# Revit family: Eurolan_Шкафы Rackcnet S3000
name_source: partatom
category: Электрооборудование
units: mm (PartAtom-declared; Revit-internal decimal feet)

## family parameters
Всегда вертикально = Да
На основе рабочей плоскости = Нет
Общий = Нет
При загрузке вырезать с полостями = Нет
Размер круглого соединителя = Использовать диаметр
Тип детали = Другая панель
Точка расчета площади = Нет

## types (64) — shared parameters
ADSK_Единица измерения = шт.
ADSK_Завод-изготовитель = Eurolan
ADSK_Количество фаз = 1
ADSK_Марка = S3000
ADSK_Материал = Металл RAL 9005
ADSK_Наименование краткое = 19'' шкаф Racknet S3000
ADSK_Напряжение = 230 В
Смещение от пола = 51 мм

## per-type parameters (varying)
| type | 33U | 42U | 47U | ADSK_Код изделия | ADSK_Масса | ADSK_Наименование | ADSK_Размер_Высота | ADSK_Размер_Глубина | ADSK_Размер_Ширина | Глубина зоны обслуживания_Сзади | Глубина зоны обслуживания_Спереди | выбор_задняя дверь | выбор_передняя дверь | число_передняя дверь |
| 22U__600 × 600_60F-22-66-30BL_19'' шкаф Racknet S3000 22U 600 × 600, передняя дверь металлическая одностворчатая, задняя дверь металлическая одностворчатая, черный | Нет | Нет | Нет | 60F-42-8A-30BL | 145 | 19'' шкаф Racknet S3000 42U 800 × 1000, передняя дверь металлическая одностворчатая, задняя дверь металлическая двустворчатая, черный | 1145 мм | 649 мм | 593 мм | 296.5 мм | 593 мм | in_Дверь_металлическая_одностворчатая | in_Дверь_металлическая_двустворчатая | 1 |
| 22U__600 × 600_60F-22-66-31BL_19'' шкаф Racknet S3000 22U 600 × 600, передняя дверь стеклянная одностворчатая, задняя дверь металлическая одностворчатая, черный | Нет | Нет | Нет | 60F-22-66-31BL | 64 | 19'' шкаф Racknet S3000 22U 600 × 600, передняя дверь стеклянная одностворчатая, задняя дверь металлическая одностворчатая, черный | 1145 мм | 649 мм | 593 мм | 296.5 мм | 593 мм | in_Дверь_металлическая_одностворчатая | in_Дверь_стеклянная_одностворчатая | 1 |
| 22U__600 × 600_60F-22-66-34BL_19'' шкаф Racknet S3000 22U 600 × 600, передняя дверь перфорированная одностворчатая, задняя дверь перфорированная одностворчатая, черный | Нет | Нет | Нет | 60F-22-66-34BL | 64 | 19'' шкаф Racknet S3000 22U 600 × 600, передняя дверь перфорированная одностворчатая, задняя дверь перфорированная одностворчатая, черный | 1145 мм | 649 мм | 593 мм | 296.5 мм | 593 мм | in_Дверь_перфорированная_одинарная | in_Дверь_перфорированная_одинарная | 1 |
| 22U__600 × 800_60F-22-68-30BL_19'' шкаф Racknet S3000 22U 600 × 800, передняя дверь металлическая одностворчатая, задняя дверь металлическая одностворчатая,  черный | Нет | Нет | Нет | 60F-22-68-30BL | 73 | 19'' шкаф Racknet S3000 22U 600 × 800, передняя дверь металлическая одностворчатая, задняя дверь металлическая одностворчатая,  черный | 1145 мм | 849 мм | 593 мм | 296.5 мм | 593 мм | in_Дверь_металлическая_одностворчатая | in_Дверь_металлическая_одностворчатая | 1 |
| 22U__600 × 800_60F-22-68-31BL_19'' шкаф Racknet S3000 22U 600 × 800, передняя дверь стеклянная одностворчатая, задняя дверь металлическая одностворчатая, черный | Нет | Нет | Нет | 60F-22-68-31BL | 73 | 19'' шкаф Racknet S3000 22U 600 × 800, передняя дверь стеклянная одностворчатая, задняя дверь металлическая одностворчатая, черный | 1145 мм | 849 мм | 593 мм | 296.5 мм | 593 мм | in_Дверь_металлическая_одностворчатая | in_Дверь_стеклянная_одностворчатая | 1 |
| 22U__600 × 800_60F-22-68-34BL_19'' шкаф Racknet S3000 22U 600 × 800, передняя дверь перфорированная одностворчатая, задняя дверь перфорированная одностворчатая, черный | Нет | Нет | Нет | 60F-22-68-34BL | 73 | 19'' шкаф Racknet S3000 22U 600 × 800, передняя дверь перфорированная одностворчатая, задняя дверь перфорированная одностворчатая, черный | 1145 мм | 849 мм | 593 мм | 296.5 мм | 593 мм | in_Дверь_перфорированная_одинарная | in_Дверь_перфорированная_одинарная | 1 |
| 22U_600 × 1000_60F-22-6A-30BL_19'' шкаф Racknet S3000 22U 600 × 1000, передняя дверь металлическая одностворчатая, задняя дверь металлическая одностворчатая, черный | Нет | Нет | Нет | 60F-22-6A-30BL | 82 | 19'' шкаф Racknet S3000 22U 600 × 1000, передняя дверь металлическая одностворчатая, задняя дверь металлическая одностворчатая, черный | 1145 мм | 1049 мм | 593 мм | 296.5 мм | 593 мм | in_Дверь_металлическая_одностворчатая | in_Дверь_металлическая_одностворчатая | 1 |
| 22U_600 × 1000_60F-22-6A-31BL_19'' шкаф Racknet S3000 22U 600 × 1000, передняя дверь стеклянная одностворчатая, задняя дверь металлическая одностворчатая, черный | Нет | Нет | Нет | 60F-22-6A-31BL | 82 | 19'' шкаф Racknet S3000 22U 600 × 1000, передняя дверь стеклянная одностворчатая, задняя дверь металлическая одностворчатая, черный | 1145 мм | 1049 мм | 593 мм | 296.5 мм | 593 мм | in_Дверь_металлическая_одностворчатая | in_Дверь_стеклянная_одностворчатая | 1 |
| 22U_600 × 1000_60F-22-6A-34BL_19'' шкаф Racknet S3000 22U 600 × 1000, передняя дверь перфорированная одностворчатая, задняя дверь перфорированная одностворчатая, черный | Нет | Нет | Нет | 60F-22-6A-34BL | 82 | 19'' шкаф Racknet S3000 22U 600 × 1000, передняя дверь перфорированная одностворчатая, задняя дверь перфорированная одностворчатая, черный | 1145 мм | 1049 мм | 593 мм | 296.5 мм | 593 мм | in_Дверь_перфорированная_одинарная | in_Дверь_перфорированная_одинарная | 1 |
| 22U_800 × 800_60F-22-88-30BL_19'' шкаф Racknet S3000 22U 800 × 800, передняя дверь металлическая одностворчатая, задняя дверь металлическая двустворчатая, черный | Нет | Нет | Нет | 60F-22-88-30BL | 78 | 19'' шкаф Racknet S3000 22U 800 × 800, передняя дверь металлическая одностворчатая, задняя дверь металлическая двустворчатая, черный | 1145 мм | 849 мм | 793 мм | 396.5 мм | 793 мм | in_Дверь_металлическая_двустворчатая | in_Дверь_металлическая_одностворчатая | 1 |
| 22U_800 × 800_60F-22-88-31BL_19'' шкаф Racknet S3000 22U 800 × 800, передняя дверь стеклянная одностворчатая, задняя дверь металлическая двустворчатая, черный | Нет | Нет | Нет | 60F-22-88-31BL | 78 | 19'' шкаф Racknet S3000 22U 800 × 800, передняя дверь стеклянная одностворчатая, задняя дверь металлическая двустворчатая, черный | 1145 мм | 849 мм | 793 мм | 396.5 мм | 793 мм | in_Дверь_металлическая_двустворчатая | in_Дверь_стеклянная_одностворчатая | 1 |
| 22U_800 × 800_60F-22-88-34BL_19'' шкаф Racknet S3000 22U 800 × 800, передняя дверь перфорированная одностворчатая, задняя дверь перфорированная двустворчатая, черный | Нет | Нет | Нет | 60F-22-88-34BL | 78 | 19'' шкаф Racknet S3000 22U 800 × 800, передняя дверь перфорированная одностворчатая, задняя дверь перфорированная двустворчатая, черный | 1145 мм | 849 мм | 793 мм | 396.5 мм | 396.5 мм | in_Дверь_перфорированная_двойная | in_Дверь_перфорированная_одинарная | 2 |
| 22U_800 × 1000_60F-22-8A-30BL_19'' шкаф Racknet S3000 22U 800 × 1000, передняя дверь металлическая одностворчатая, задняя дверь металлическая двустворчатая, черный | Нет | Нет | Нет | 60F-22-8A-30BL | 86 | 19'' шкаф Racknet S3000 22U 800 × 1000, передняя дверь металлическая одностворчатая, задняя дверь металлическая двустворчатая, черный | 1145 мм | 1049 мм | 793 мм | 396.5 мм | 793 мм | in_Дверь_металлическая_двустворчатая | in_Дверь_металлическая_одностворчатая | 1 |
| 22U_800 × 1000_60F-22-8A-31BL_19'' шкаф Racknet S3000 22U 800 × 1000, передняя дверь стеклянная одностворчатая, задняя дверь металлическая двустворчатая, черный | Нет | Нет | Нет | 60F-22-8A-31BL | 86 | 19'' шкаф Racknet S3000 22U 800 × 1000, передняя дверь стеклянная одностворчатая, задняя дверь металлическая двустворчатая, черный | 1145 мм | 1049 мм | 793 мм | 396.5 мм | 793 мм | in_Дверь_металлическая_двустворчатая | in_Дверь_стеклянная_одностворчатая | 1 |
| 22U_800 × 1000_60F-22-8A-34BL_19'' шкаф Racknet S3000 22U 800 × 1000, передняя дверь перфорированная одностворчатая, задняя дверь перфорированная двустворчатая, черный | Нет | Нет | Нет | 60F-22-8A-34BL | 86 | 19'' шкаф Racknet S3000 22U 800 × 1000, передняя дверь перфорированная одностворчатая, задняя дверь перфорированная двустворчатая, черный | 1145 мм | 1049 мм | 793 мм | 396.5 мм | 793 мм | in_Дверь_перфорированная_двойная | in_Дверь_перфорированная_одинарная | 1 |
| 33U__600 × 600_60F-33-66-30BL_19'' шкаф Racknet S3000 33U 600 × 600, передняя дверь металлическая одностворчатая, задняя дверь металлическая одностворчатая, черный | Да | Нет | Нет | 60F-33-66-30BL | 86 | 19'' шкаф Racknet S3000 33U 600 × 600, передняя дверь металлическая одностворчатая, задняя дверь металлическая одностворчатая, черный | 1633 мм | 649 мм | 593 мм | 296.5 мм | 593 мм | in_Дверь_металлическая_одностворчатая | in_Дверь_металлическая_одностворчатая | 1 |
| 33U__600 × 600_60F-33-66-31BL_19'' шкаф Racknet S3000 33U 600 × 600, передняя дверь стеклянная одностворчатая, задняя дверь металлическая одностворчатая, черный | Да | Нет | Нет | 60F-33-66-31BL | 86 | 19'' шкаф Racknet S3000 33U 600 × 600, передняя дверь стеклянная одностворчатая, задняя дверь металлическая одностворчатая, черный | 1633 мм | 649 мм | 593 мм | 296.5 мм | 593 мм | in_Дверь_металлическая_одностворчатая | in_Дверь_стеклянная_одностворчатая | 1 |
| 33U__600 × 600_60F-33-66-34BL_19'' шкаф Racknet S3000 33U 600 × 600, передняя дверь перфорированная одностворчатая, задняя дверь перфорированная одностворчатая, черный | Да | Нет | Нет | 60F-33-66-34BL | 86 | 19'' шкаф Racknet S3000 33U 600 × 600, передняя дверь перфорированная одностворчатая, задняя дверь перфорированная одностворчатая, черный | 1633 мм | 649 мм | 593 мм | 296.5 мм | 593 мм | in_Дверь_перфорированная_одинарная | in_Дверь_перфорированная_одинарная | 1 |
| 33U__600 × 800_60F-33-68-30BL_19'' шкаф Racknet S3000 33U 600 × 800, передняя дверь металлическая одностворчатая, задняя дверь металлическая одностворчатая,  черный | Да | Нет | Нет | 60F-33-68-30BL | 100 | 19'' шкаф Racknet S3000 33U 600 × 800, передняя дверь металлическая одностворчатая, задняя дверь металлическая одностворчатая,  черный | 1633 мм | 849 мм | 593 мм | 296.5 мм | 593 мм | in_Дверь_металлическая_одностворчатая | in_Дверь_металлическая_одностворчатая | 1 |
| 33U__600 × 800_60F-33-68-31BL_19'' шкаф Racknet S3000 33U 600 × 800, передняя дверь стеклянная одностворчатая, задняя дверь металлическая одностворчатая, черный | Да | Нет | Нет | 60F-33-68-31BL | 100 | 19'' шкаф Racknet S3000 33U 600 × 800, передняя дверь стеклянная одностворчатая, задняя дверь металлическая одностворчатая, черный | 1633 мм | 849 мм | 593 мм | 296.5 мм | 593 мм | in_Дверь_металлическая_одностворчатая | in_Дверь_стеклянная_одностворчатая | 1 |
| 33U__600 × 800_60F-33-68-34BL_19'' шкаф Racknet S3000 33U 600 × 800, передняя дверь перфорированная одностворчатая, задняя дверь перфорированная одностворчатая, черный | Да | Нет | Нет | 60F-33-68-34BL | 100 | 19'' шкаф Racknet S3000 33U 600 × 800, передняя дверь перфорированная одностворчатая, задняя дверь перфорированная одностворчатая, черный | 1633 мм | 849 мм | 593 мм | 296.5 мм | 593 мм | in_Дверь_перфорированная_одинарная | in_Дверь_перфорированная_одинарная | 1 |
| 33U_600 × 1000_60F-33-6A-30BL_19'' шкаф Racknet S3000 33U 600 × 1000, передняя дверь металлическая одностворчатая, задняя дверь металлическая одностворчатая, черный | Да | Нет | Нет | 60F-33-6A-30BL | 114 | 19'' шкаф Racknet S3000 33U 600 × 1000, передняя дверь металлическая одностворчатая, задняя дверь металлическая одностворчатая, черный | 1633 мм | 1049 мм | 593 мм | 296.5 мм | 593 мм | in_Дверь_металлическая_одностворчатая | in_Дверь_металлическая_одностворчатая | 1 |
| 33U_600 × 1000_60F-33-6A-31BL_19'' шкаф Racknet S3000 33U 600 × 1000, передняя дверь стеклянная одностворчатая, задняя дверь металлическая одностворчатая, черный | Да | Нет | Нет | 60F-33-6A-31BL | 114 | 19'' шкаф Racknet S3000 33U 600 × 1000, передняя дверь стеклянная одностворчатая, задняя дверь металлическая одностворчатая, черный | 1633 мм | 1049 мм | 593 мм | 296.5 мм | 593 мм | in_Дверь_металлическая_одностворчатая | in_Дверь_стеклянная_одностворчатая | 1 |
| 33U_600 × 1000_60F-33-6A-34BL_19'' шкаф Racknet S3000 33U 600 × 1000, передняя дверь перфорированная одностворчатая, задняя дверь перфорированная одностворчатая, черный | Да | Нет | Нет | 60F-33-6A-34BL | 114 | 19'' шкаф Racknet S3000 33U 600 × 1000, передняя дверь перфорированная одностворчатая, задняя дверь перфорированная одностворчатая, черный | 1633 мм | 1049 мм | 593 мм | 296.5 мм | 593 мм | in_Дверь_перфорированная_одинарная | in_Дверь_перфорированная_одинарная | 1 |
| 33U_800 × 800_60F-33-88-30BL_19'' шкаф Racknet S3000 33U 800 × 800, передняя дверь металлическая одностворчатая, задняя дверь металлическая двустворчатая, черный | Да | Нет | Нет | 60F-33-88-30BL | 110 | 19'' шкаф Racknet S3000 33U 800 × 800, передняя дверь металлическая одностворчатая, задняя дверь металлическая двустворчатая, черный | 1633 мм | 849 мм | 793 мм | 396.5 мм | 793 мм | in_Дверь_металлическая_двустворчатая | in_Дверь_металлическая_одностворчатая | 1 |
| 33U_800 × 800_60F-33-88-31BL_19'' шкаф Racknet S3000 33U 800 × 800, передняя дверь стеклянная одностворчатая, задняя дверь металлическая двустворчатая, черный | Да | Нет | Нет | 60F-33-88-31BL | 110 | 19'' шкаф Racknet S3000 33U 800 × 800, передняя дверь стеклянная одностворчатая, задняя дверь металлическая двустворчатая, черный | 1633 мм | 849 мм | 793 мм | 396.5 мм | 793 мм | in_Дверь_металлическая_двустворчатая | in_Дверь_стеклянная_одностворчатая | 1 |
| 33U_800 × 800_60F-33-88-34BL_19'' шкаф Racknet S3000 33U 800 × 800, передняя дверь перфорированная одностворчатая, задняя дверь перфорированная двустворчатая, черный | Да | Нет | Нет | 60F-33-88-34BL | 110 | 19'' шкаф Racknet S3000 33U 800 × 800, передняя дверь перфорированная одностворчатая, задняя дверь перфорированная двустворчатая, черный | 1633 мм | 849 мм | 793 мм | 396.5 мм | 793 мм | in_Дверь_перфорированная_двойная | in_Дверь_перфорированная_одинарная | 1 |
| 33U_800 × 1000_60F-33-8A-30BL_19'' шкаф Racknet S3000 33U 800 × 1000, передняя дверь металлическая одностворчатая, задняя дверь металлическая двустворчатая, черный | Да | Нет | Нет | 60F-33-8A-30BL | 125 | 19'' шкаф Racknet S3000 33U 800 × 1000, передняя дверь металлическая одностворчатая, задняя дверь металлическая двустворчатая, черный | 1633 мм | 1049 мм | 793 мм | 396.5 мм | 793 мм | in_Дверь_металлическая_двустворчатая | in_Дверь_металлическая_одностворчатая | 1 |
| 33U_800 × 1000_60F-33-8A-31BL_19'' шкаф Racknet S3000 33U 800 × 1000, передняя дверь стеклянная одностворчатая, задняя дверь металлическая двустворчатая, черный | Да | Нет | Нет | 60F-33-8A-31BL | 125 | 19'' шкаф Racknet S3000 33U 800 × 1000, передняя дверь стеклянная одностворчатая, задняя дверь металлическая двустворчатая, черный | 1633 мм | 1049 мм | 793 мм | 396.5 мм | 793 мм | in_Дверь_металлическая_двустворчатая | in_Дверь_стеклянная_одностворчатая | 1 |
| 33U_800 × 1000_60F-33-8A-34BL_19'' шкаф Racknet S3000 33U 800 × 1000, передняя дверь перфорированная одностворчатая, задняя дверь перфорированная двустворчатая, черный | Да | Нет | Нет | 60F-33-8A-34BL | 125 | 19'' шкаф Racknet S3000 33U 800 × 1000, передняя дверь перфорированная одностворчатая, задняя дверь перфорированная двустворчатая, черный | 1633 мм | 1049 мм | 793 мм | 396.5 мм | 793 мм | in_Дверь_перфорированная_двойная | in_Дверь_перфорированная_одинарная | 1 |
| 42U__600 × 600_60F-42-66-30BL_19'' шкаф Racknet S3000 42U 600 × 600, передняя дверь металлическая одностворчатая, задняя дверь металлическая одностворчатая, черный | Да | Да | Нет | 60F-42-66-30BL | 105 | 19'' шкаф Racknet S3000 42U 600 × 600, передняя дверь металлическая одностворчатая, задняя дверь металлическая одностворчатая, черный | 2034 мм | 649 мм | 593 мм | 296.5 мм | 593 мм | in_Дверь_металлическая_одностворчатая | in_Дверь_металлическая_одностворчатая | 1 |
| 42U__600 × 600_60F-42-66-31BL_19'' шкаф Racknet S3000 42U 600 × 600, передняя дверь стеклянная одностворчатая, задняя дверь металлическая одностворчатая, черный | Да | Да | Нет | 60F-42-66-31BL | 105 | 19'' шкаф Racknet S3000 42U 600 × 600, передняя дверь стеклянная одностворчатая, задняя дверь металлическая одностворчатая, черный | 2034 мм | 649 мм | 593 мм | 296.5 мм | 593 мм | in_Дверь_металлическая_одностворчатая | in_Дверь_стеклянная_одностворчатая | 1 |
| 42U__600 × 600_60F-42-66-34BL_19'' шкаф Racknet S3000 42U 600 × 600, передняя дверь перфорированная одностворчатая, задняя дверь перфорированная одностворчатая, черный | Да | Да | Нет | 60F-42-66-34BL | 105 | 19'' шкаф Racknet S3000 42U 600 × 600, передняя дверь перфорированная одностворчатая, задняя дверь перфорированная одностворчатая, черный | 2034 мм | 649 мм | 593 мм | 296.5 мм | 593 мм | in_Дверь_перфорированная_одинарная | in_Дверь_перфорированная_одинарная | 1 |
| 42U__600 × 800_60F-42-68-30BL_19'' шкаф Racknet S3000 42U 600 × 800, передняя дверь металлическая одностворчатая, задняя дверь металлическая одностворчатая,  черный | Да | Да | Нет | 60F-42-68-30BL | 119 | 19'' шкаф Racknet S3000 42U 600 × 800, передняя дверь металлическая одностворчатая, задняя дверь металлическая одностворчатая, черный | 2034 мм | 849 мм | 593 мм | 296.5 мм | 593 мм | in_Дверь_металлическая_одностворчатая | in_Дверь_металлическая_одностворчатая | 1 |
| 42U__600 × 800_60F-42-68-31BL_19'' шкаф Racknet S3000 42U 600 × 800, передняя дверь стеклянная одностворчатая, задняя дверь металлическая одностворчатая, черный | Да | Да | Нет | 60F-42-68-31BL | 119 | 19'' шкаф Racknet S3000 42U 600 × 800, передняя дверь стеклянная одностворчатая, задняя дверь металлическая одностворчатая, черный | 2034 мм | 849 мм | 593 мм | 296.5 мм | 593 мм | in_Дверь_металлическая_одностворчатая | in_Дверь_стеклянная_одностворчатая | 1 |
| 42U__600 × 800_60F-42-68-34BL_19'' шкаф Racknet S3000 42U 600 × 800, передняя дверь перфорированная одностворчатая, задняя дверь перфорированная одностворчатая, черный | Да | Да | Нет | 60F-42-68-34BL | 119 | 19'' шкаф Racknet S3000 42U 600 × 800, передняя дверь перфорированная одностворчатая, задняя дверь перфорированная одностворчатая, черный | 2034 мм | 849 мм | 593 мм | 296.5 мм | 593 мм | in_Дверь_перфорированная_одинарная | in_Дверь_перфорированная_одинарная | 1 |
| 42U_600 × 1000_60F-42-6A-30BL_19'' шкаф Racknet S3000 42U 600 × 1000, передняя дверь металлическая одностворчатая, задняя дверь металлическая одностворчатая, черный | Да | Да | Нет | 60F-42-6A-30BL | 133 | 19'' шкаф Racknet S3000 42U 600 × 1000, передняя дверь металлическая одностворчатая, задняя дверь металлическая одностворчатая, черный | 2034 мм | 1049 мм | 593 мм | 296.5 мм | 593 мм | in_Дверь_металлическая_одностворчатая | in_Дверь_металлическая_одностворчатая | 1 |
| 42U_600 × 1000_60F-42-6A-31BL_19'' шкаф Racknet S3000 42U 600 × 1000, передняя дверь стеклянная одностворчатая, задняя дверь металлическая одностворчатая, черный | Да | Да | Нет | 60F-42-6A-31BL | 133 | 19'' шкаф Racknet S3000 42U 600 × 1000, передняя дверь стеклянная одностворчатая, задняя дверь металлическая одностворчатая, черный | 2034 мм | 1049 мм | 593 мм | 296.5 мм | 593 мм | in_Дверь_металлическая_одностворчатая | in_Дверь_стеклянная_одностворчатая | 1 |
| 42U_600 × 1000_60F-42-6A-34BL_19'' шкаф Racknet S3000 42U 600 × 1000, передняя дверь перфорированная одностворчатая, задняя дверь перфорированная одностворчатая, черный | Да | Да | Нет | 60F-42-6A-34BL | 133 | 19'' шкаф Racknet S3000 42U 600 × 1000, передняя дверь перфорированная одностворчатая, задняя дверь перфорированная одностворчатая, черный | 2034 мм | 1049 мм | 593 мм | 296.5 мм | 593 мм | in_Дверь_перфорированная_одинарная | in_Дверь_перфорированная_одинарная | 1 |
| 42U_800 × 800_60F-42-88-30BL_19'' шкаф Racknet S3000 42U 800 × 800, передняя дверь металлическая одностворчатая, задняя дверь металлическая двустворчатая, черный | Да | Да | Нет | 60F-42-88-30BL | 130 | 19'' шкаф Racknet S3000 42U 800 × 800, передняя дверь металлическая одностворчатая, задняя дверь металлическая двустворчатая, черный | 2034 мм | 849 мм | 793 мм | 396.5 мм | 793 мм | in_Дверь_металлическая_двустворчатая | in_Дверь_металлическая_одностворчатая | 1 |
| 42U_800 × 800_60F-42-88-31BL_19'' шкаф Racknet S3000 42U 800 × 800, передняя дверь стеклянная одностворчатая, задняя дверь металлическая двустворчатая, черный | Да | Да | Нет | 60F-42-88-31BL | 130 | 19'' шкаф Racknet S3000 42U 800 × 800, передняя дверь стеклянная одностворчатая, задняя дверь металлическая двустворчатая, черный | 2034 мм | 849 мм | 793 мм | 396.5 мм | 793 мм | in_Дверь_металлическая_двустворчатая | in_Дверь_стеклянная_одностворчатая | 1 |
| 42U_800 × 800_60F-42-88-34BL_19'' шкаф Racknet S3000 42U 800 × 800, передняя дверь перфорированная одностворчатая, задняя дверь перфорированная двустворчатая, черный | Да | Да | Нет | 60F-42-88-34BL | 130 | 19'' шкаф Racknet S3000 42U 800 × 800, передняя дверь перфорированная одностворчатая, задняя дверь перфорированная двустворчатая, черный | 2034 мм | 849 мм | 793 мм | 396.5 мм | 793 мм | in_Дверь_перфорированная_двойная | in_Дверь_перфорированная_одинарная | 1 |
| 42U_800 × 800_60F-42-88-35BL_19'' шкаф Racknet S3000 42U 800 × 800, передняя дверь перфорированная двустворчатая, задняя дверь перфорированная двустворчатая, черный | Да | Да | Нет | 60F-42-88-35BL | 130 | 19'' шкаф Racknet S3000 42U 800 × 800, передняя дверь перфорированная двустворчатая, задняя дверь перфорированная двустворчатая, черный | 2034 мм | 849 мм | 793 мм | 396.5 мм | 396.5 мм | in_Дверь_перфорированная_двойная | in_Дверь_перфорированная_двойная | 2 |
| 42U_800 × 1000_60F-42-8A-30BL_19'' шкаф Racknet S3000 42U 800 × 1000, передняя дверь металлическая одностворчатая, задняя дверь металлическая двустворчатая, черный | Да | Да | Нет | 60F-42-8A-30BL | 145 | 19'' шкаф Racknet S3000 42U 800 × 1000, передняя дверь металлическая одностворчатая, задняя дверь металлическая двустворчатая, черный | 2034 мм | 1049 мм | 793 мм | 396.5 мм | 793 мм | in_Дверь_металлическая_одностворчатая | in_Дверь_металлическая_двустворчатая | 1 |
| 42U_800 × 1000_60F-42-8A-31BL_19'' шкаф Racknet S3000 42U 800 × 1000, передняя дверь стеклянная одностворчатая, задняя дверь металлическая двустворчатая, черный | Да | Да | Нет | 60F-42-8A-31BL | 145 | 19'' шкаф Racknet S3000 42U 800 × 1000, передняя дверь стеклянная одностворчатая, задняя дверь металлическая двустворчатая, черный | 2034 мм | 1049 мм | 793 мм | 396.5 мм | 793 мм | in_Дверь_металлическая_двустворчатая | in_Дверь_стеклянная_одностворчатая | 1 |
| 42U_800 × 1000_60F-42-8A-34BL_19'' шкаф Racknet S3000 42U 800 × 1000, передняя дверь перфорированная одностворчатая, задняя дверь перфорированная двустворчатая, черный | Да | Да | Нет | 60F-42-8A-34BL | 145 | 19'' шкаф Racknet S3000 42U 800 × 1000, передняя дверь перфорированная одностворчатая, задняя дверь перфорированная двустворчатая, черный | 2034 мм | 1049 мм | 793 мм | 396.5 мм | 793 мм | in_Дверь_перфорированная_двойная | in_Дверь_перфорированная_одинарная | 1 |
| 42U_800 × 1000_60F-42-8A-35BL_19'' шкаф Racknet S3000 42U 800 × 1000, передняя дверь перфорированная двустворчатая, задняя дверь перфорированная двустворчатая, черный | Да | Да | Нет | 60F-42-8A-35BL | 145 | 19'' шкаф Racknet S3000 42U 800 × 1000, передняя дверь перфорированная двустворчатая, задняя дверь перфорированная двустворчатая, черный | 2034 мм | 1049 мм | 793 мм | 396.5 мм | 396.5 мм | in_Дверь_перфорированная_двойная | in_Дверь_перфорированная_двойная | 2 |
| 47U__600 × 600_60F-47-66-30BL_19'' шкаф Racknet S3000 47U 600 × 600, передняя дверь металлическая одностворчатая, задняя дверь металлическая одностворчатая, черный | Да | Да | Да | 60F-47-66-30BL | 114 | 19'' шкаф Racknet S3000 47U 600 × 600, передняя дверь металлическая одностворчатая, задняя дверь металлическая одностворчатая, черный | 2257 мм | 649 мм | 593 мм | 296.5 мм | 593 мм | in_Дверь_металлическая_одностворчатая | in_Дверь_металлическая_одностворчатая | 1 |
| 47U__600 × 600_60F-47-66-31BL_19'' шкаф Racknet S3000 47U 600 × 600, передняя дверь стеклянная одностворчатая, задняя дверь металлическая одностворчатая, черный | Да | Да | Да | 60F-47-66-31BL | 114 | 19'' шкаф Racknet S3000 47U 600 × 600, передняя дверь стеклянная одностворчатая, задняя дверь металлическая одностворчатая, черный | 2257 мм | 649 мм | 593 мм | 296.5 мм | 593 мм | in_Дверь_металлическая_одностворчатая | in_Дверь_стеклянная_одностворчатая | 1 |
| 47U__600 × 600_60F-47-66-34BL_19'' шкаф Racknet S3000 47U 600 × 600, передняя дверь перфорированная одностворчатая, задняя дверь перфорированная одностворчатая, черный | Да | Да | Да | 60F-47-66-34BL | 114 | 19'' шкаф Racknet S3000 47U 600 × 600, передняя дверь перфорированная одностворчатая, задняя дверь перфорированная одностворчатая, черный | 2257 мм | 649 мм | 593 мм | 296.5 мм | 593 мм | in_Дверь_перфорированная_одинарная | in_Дверь_перфорированная_одинарная | 1 |
| 47U__600 × 800_60F-47-68-30BL_19'' шкаф Racknet S3000 47U 600 × 800, передняя дверь металлическая одностворчатая, задняя дверь металлическая одностворчатая,  черный | Да | Да | Да | 60F-47-68-30BL | 129 | 19'' шкаф Racknet S3000 47U 600 × 800, передняя дверь металлическая одностворчатая, задняя дверь металлическая одностворчатая,  черный | 2257 мм | 849 мм | 593 мм | 296.5 мм | 593 мм | in_Дверь_металлическая_одностворчатая | in_Дверь_металлическая_одностворчатая | 1 |
| 47U__600 × 800_60F-47-68-31BL_19'' шкаф Racknet S3000 47U 600 × 800, передняя дверь стеклянная одностворчатая, задняя дверь металлическая одностворчатая, черный | Да | Да | Да | 60F-47-68-31BL | 129 | 19'' шкаф Racknet S3000 47U 600 × 800, передняя дверь стеклянная одностворчатая, задняя дверь металлическая одностворчатая, черный | 2257 мм | 849 мм | 593 мм | 296.5 мм | 593 мм | in_Дверь_металлическая_одностворчатая | in_Дверь_стеклянная_одностворчатая | 1 |
| 47U__600 × 800_60F-47-68-34BL_19'' шкаф Racknet S3000 47U 600 × 800, передняя дверь перфорированная одностворчатая, задняя дверь перфорированная одностворчатая, черный | Да | Да | Да | 60F-47-68-34BL | 129 | 19'' шкаф Racknet S3000 47U 600 × 800, передняя дверь перфорированная одностворчатая, задняя дверь перфорированная одностворчатая, черный | 2257 мм | 849 мм | 593 мм | 296.5 мм | 593 мм | in_Дверь_перфорированная_одинарная | in_Дверь_перфорированная_одинарная | 1 |
| 47U_600 × 1000_60F-47-6A-30BL_19'' шкаф Racknet S3000 47U 600 × 1000, передняя дверь металлическая одностворчатая, задняя дверь металлическая одностворчатая, черный | Да | Да | Да | 60F-47-6A-30BL | 143 | 19'' шкаф Racknet S3000 47U 600 × 1000, передняя дверь металлическая одностворчатая, задняя дверь металлическая одностворчатая, черный | 2257 мм | 1049 мм | 593 мм | 296.5 мм | 593 мм | in_Дверь_металлическая_одностворчатая | in_Дверь_металлическая_одностворчатая | 1 |
| 47U_600 × 1000_60F-47-6A-31BL_19'' шкаф Racknet S3000 47U 600 × 1000, передняя дверь стеклянная одностворчатая, задняя дверь металлическая одностворчатая, черный | Да | Да | Да | 60F-47-6A-31BL | 143 | 19'' шкаф Racknet S3000 47U 600 × 1000, передняя дверь стеклянная одностворчатая, задняя дверь металлическая одностворчатая, черный | 2257 мм | 1049 мм | 593 мм | 296.5 мм | 593 мм | in_Дверь_металлическая_одностворчатая | in_Дверь_стеклянная_одностворчатая | 1 |
| 47U_600 × 1000_60F-47-6A-34BL_19'' шкаф Racknet S3000 47U 600 × 1000, передняя дверь перфорированная одностворчатая, задняя дверь перфорированная одностворчатая, черный | Да | Да | Да | 60F-47-6A-34BL | 143 | 19'' шкаф Racknet S3000 47U 600 × 1000, передняя дверь перфорированная одностворчатая, задняя дверь перфорированная одностворчатая, черный | 2257 мм | 1049 мм | 593 мм | 296.5 мм | 593 мм | in_Дверь_перфорированная_одинарная | in_Дверь_перфорированная_одинарная | 1 |
| 47U_800 × 800_60F-47-88-30BL_19'' шкаф Racknet S3000 47U 800 × 800, передняя дверь металлическая одностворчатая, задняя дверь металлическая двустворчатая, черный | Да | Да | Да | 60F-47-88-30BL | 140 | 19'' шкаф Racknet S3000 47U 800 × 800, передняя дверь металлическая одностворчатая, задняя дверь металлическая двустворчатая, черный | 2257 мм | 849 мм | 793 мм | 396.5 мм | 793 мм | in_Дверь_металлическая_двустворчатая | in_Дверь_металлическая_одностворчатая | 1 |
| 47U_800 × 800_60F-47-88-31BL_19'' шкаф Racknet S3000 47U 800 × 800, передняя дверь стеклянная одностворчатая, задняя дверь металлическая двустворчатая, черный | Да | Да | Да | 60F-47-88-31BL | 140 | 19'' шкаф Racknet S3000 47U 800 × 800, передняя дверь стеклянная одностворчатая, задняя дверь металлическая двустворчатая, черный | 2257 мм | 849 мм | 793 мм | 396.5 мм | 793 мм | in_Дверь_металлическая_двустворчатая | in_Дверь_стеклянная_одностворчатая | 1 |
| 47U_800 × 800_60F-47-88-34BL_19'' шкаф Racknet S3000 47U 800 × 800, передняя дверь перфорированная одностворчатая, задняя дверь перфорированная двустворчатая, черный | Да | Да | Да | 60F-47-88-34BL | 140 | 19'' шкаф Racknet S3000 47U 800 × 800, передняя дверь перфорированная одностворчатая, задняя дверь перфорированная двустворчатая, черный | 2257 мм | 849 мм | 793 мм | 396.5 мм | 793 мм | in_Дверь_перфорированная_двойная | in_Дверь_перфорированная_одинарная | 1 |
| 47U_800 × 800_60F-47-88-35BL_19'' шкаф Racknet S3000 47U 800 × 800, передняя дверь перфорированная двустворчатая, задняя дверь перфорированная двустворчатая, черный | Да | Да | Да | 60F-47-88-35BL | 140 | 19'' шкаф Racknet S3000 47U 800 × 800, передняя дверь перфорированная двустворчатая, задняя дверь перфорированная двустворчатая, черный | 2257 мм | 849 мм | 793 мм | 396.5 мм | 396.5 мм | in_Дверь_перфорированная_двойная | in_Дверь_перфорированная_двойная | 2 |
| 47U_800 × 1000_60F-47-8A-30BL_19'' шкаф Racknet S3000 47U 800 × 1000, передняя дверь металлическая одностворчатая, задняя дверь металлическая двустворчатая, черный | Да | Да | Да | 60F-47-8A-30BL | 155 | 19'' шкаф Racknet S3000 47U 800 × 1000, передняя дверь металлическая одностворчатая, задняя дверь металлическая двустворчатая, черный | 2257 мм | 1049 мм | 793 мм | 396.5 мм | 793 мм | in_Дверь_металлическая_двустворчатая | in_Дверь_металлическая_одностворчатая | 1 |
| 47U_800 × 1000_60F-47-8A-31BL_19'' шкаф Racknet S3000 47U 800 × 1000, передняя дверь стеклянная одностворчатая, задняя дверь металлическая двустворчатая, черный | Да | Да | Да | 60F-47-8A-31BL | 155 | 19'' шкаф Racknet S3000 47U 800 × 1000, передняя дверь стеклянная одностворчатая, задняя дверь металлическая двустворчатая, черный | 2257 мм | 1049 мм | 793 мм | 396.5 мм | 793 мм | in_Дверь_металлическая_двустворчатая | in_Дверь_стеклянная_одностворчатая | 1 |
| 47U_800 × 1000_60F-47-8A-34BL_19'' шкаф Racknet S3000 47U 800 × 1000, передняя дверь перфорированная одностворчатая, задняя дверь перфорированная двустворчатая, черный | Да | Да | Да | 60F-47-8A-34BL | 155 | 19'' шкаф Racknet S3000 47U 800 × 1000, передняя дверь перфорированная одностворчатая, задняя дверь перфорированная двустворчатая, черный | 2257 мм | 1049 мм | 793 мм | 396.5 мм | 793 мм | in_Дверь_перфорированная_двойная | in_Дверь_перфорированная_одинарная | 1 |
| 47U_800 × 1000_60F-47-8A-35BL_19'' шкаф Racknet S3000 47U 800 × 1000, передняя дверь перфорированная двустворчатая, задняя дверь перфорированная двустворчатая, черный | Да | Да | Да | 60F-47-8A-35BL | 155 | 19'' шкаф Racknet S3000 47U 800 × 1000, передняя дверь перфорированная двустворчатая, задняя дверь перфорированная двустворчатая, черный | 2257 мм | 1049 мм | 793 мм | 396.5 мм | 396.5 мм | in_Дверь_перфорированная_двойная | in_Дверь_перфорированная_двойная | 2 |
